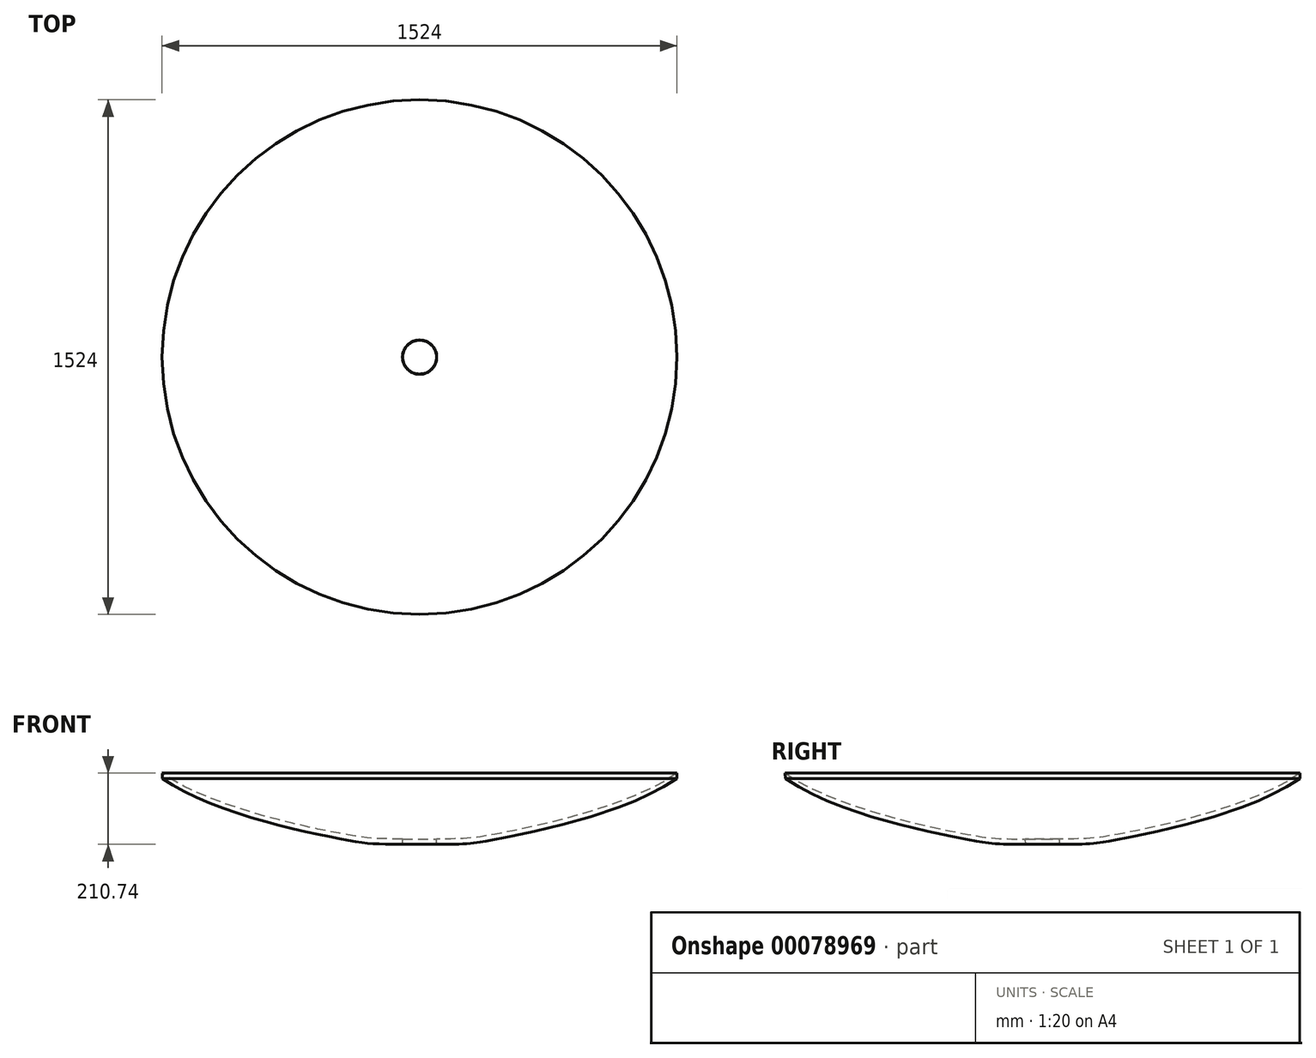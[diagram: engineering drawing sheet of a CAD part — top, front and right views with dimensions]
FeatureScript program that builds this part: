
annotation { "Feature Type Name" : "Feature", "Feature Type Description" : "" }
export const myFeature = defineFeature(function(context is Context, id is Id, definition is map)
    precondition{}
    {
        {
            var Q0;
            Q0=qCreatedBy(makeId("Front.planeOp"),FACE);
            var sketch = newSketch(context, id + "F0", { "sketchPlane" : qUnion([Q0])});
            skFitSpline(sketch, "E0", {"points": [v(50.8, 0) * mm, v(210.54, 11.91) * mm, v(762, 194.88) * mm], "startDerivative": vector(712.47, 6.11) * mm, "endDerivative": vector(660.42, 466.54) * mm});
            skFitSpline(sketch, "E1", {"points": [v(49.87, -15.86) * mm, v(209.61, -3.95) * mm, v(761.07, 179.02) * mm], "startDerivative": vector(712.47, 6.11) * mm, "endDerivative": vector(660.42, 466.54) * mm});
            skLineSegment(sketch, "E2", {"start": v(49.87, -15.86) * mm, "end": v(50.8, 0) * mm});
            skLineSegment(sketch, "E3", {"start": v(761.07, 179.02) * mm, "end": v(762, 194.88) * mm});
            skSolve(sketch);
        }
        {
            var Q0;
            Q0=qCreatedBy(makeId("Front.planeOp"),FACE);
            var sketch = newSketch(context, id + "F1", { "sketchPlane" : qUnion([Q0])});
            skLineSegment(sketch, "E4", {"start": v(0, 0) * mm, "end": v(0, 211.1) * mm, "construction": true});
            skSolve(sketch);
        }
        {
            var Q0;
            Q0 = qSketchRegion(id + "F0", true);
            var Q1;
            Q1=sQuery(id+"F1.wireOp",EDGE,"E4");
            revolve(context, id + "F2", {"entities" : qUnion([Q0]), "axis" : qUnion([Q1]), "revolveType" : RevolveType.FULL});
        }
    });
